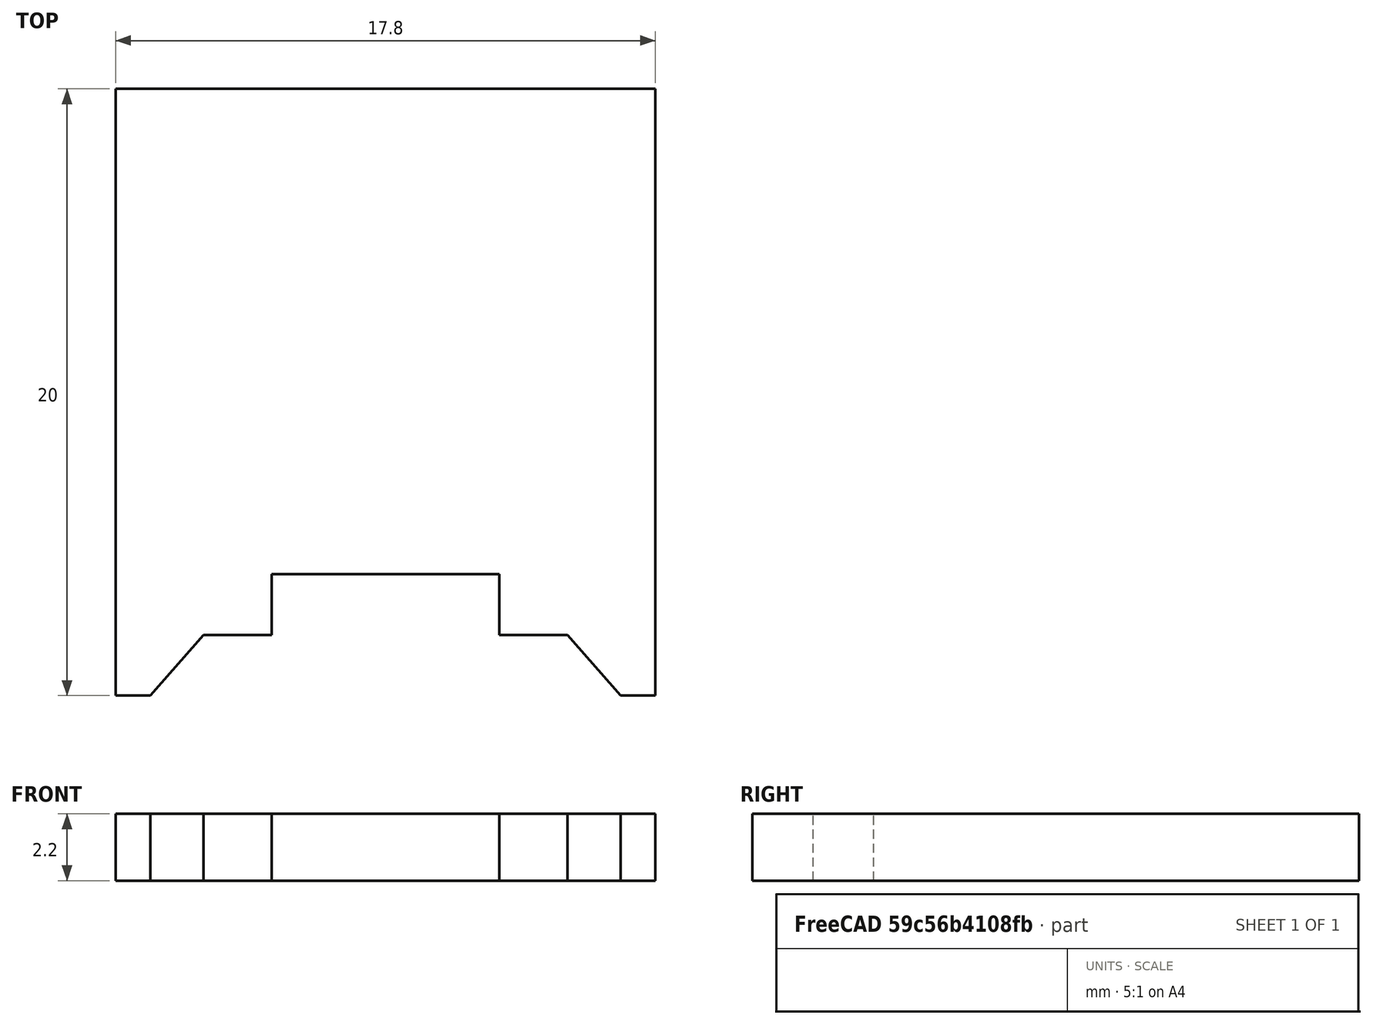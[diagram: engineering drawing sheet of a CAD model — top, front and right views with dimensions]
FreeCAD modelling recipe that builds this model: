
FCSTD DOCUMENT  (FreeCAD 0.19R)
Label: rs41 upper mark 3
License: All rights reserved
LicenseURL: http://en.wikipedia.org/wiki/All_rights_reserved
objects: Sketcher::SketchObject×1, PartDesign::Pad×1, PartDesign::Body×1
note: 4 computed .brp shape members not serialized (recipe doc carries the construction recipe); baked Part::Feature solids carry a one-line shape summary decoded from their .brp

FEATURE [Sketcher::SketchObject] Sketch
  FullyConstrained = true
  MapMode = 5
  Support = -> [XY_Plane]
  sketch-geometry (12):
    g0: LineSegment StartX=-3.75 StartY=-16 StartZ=0 EndX=3.75 EndY=-16 EndZ=0
    g1: LineSegment StartX=3.75 StartY=-16 StartZ=0 EndX=3.75 EndY=-18 EndZ=0
    g2: LineSegment StartX=3.75 StartY=-18 StartZ=0 EndX=6 EndY=-18 EndZ=0
    g3: LineSegment StartX=7.75 StartY=-20 StartZ=0 EndX=8.9 EndY=-20 EndZ=0
    g4: LineSegment StartX=-8.9 StartY=0 StartZ=0 EndX=-8.9 EndY=-20 EndZ=0
    g5: LineSegment StartX=-8.9 StartY=-20 StartZ=0 EndX=-7.75 EndY=-20 EndZ=0
    g6: LineSegment StartX=-7.75 StartY=-20 StartZ=0 EndX=-6 EndY=-18 EndZ=0
    g7: LineSegment StartX=-6 StartY=-18 StartZ=0 EndX=-3.75 EndY=-18 EndZ=0
    g8: LineSegment StartX=-3.75 StartY=-18 StartZ=0 EndX=-3.75 EndY=-16 EndZ=0
    g9: LineSegment StartX=6 StartY=-18 StartZ=0 EndX=7.75 EndY=-20 EndZ=0
    g10: LineSegment StartX=8.9 StartY=-20 StartZ=0 EndX=8.9 EndY=0 EndZ=0
    g11: LineSegment StartX=8.9 StartY=0 StartZ=0 EndX=-8.9 EndY=0 EndZ=0
  constraints (30):
    c: Coincident(g1,g0)
    c: Vertical(g1)
    c: Horizontal(g2)
    c: Horizontal(g3)
    c: Vertical(g4)
    c: Coincident(g5,g4)
    c: Coincident(g6,g5)
    c: Coincident(g7,g6)
    c: Coincident(g8,g7)
    c: Coincident(g8,g0)
    c: Coincident(g2,g1)
    c: Coincident(g9,g2)
    c: Coincident(g9,g3)
    c: Coincident(g10,g3)
    c: Coincident(g11,g10)
    c: Symmetric(g4,g10,g-2)
    c: Symmetric(g4,g3,g-2)
    c: Symmetric(g5,g3,g-2)
    c: Symmetric(g6,g2,g-2)
    c: Symmetric(g7,g1,g-2)
    c: Distance(g0) = 7.5
    c: DistanceX(g4,g10) = 17.8
    c: Distance(g8) = 2
    c: DistanceX(g6,g2) = 12
    c: DistanceX(g5,g3) = 15.5
    c: Distance(g10) = 20
    c: Symmetric(g0,g0,g-2)
    c: DistanceY(g3,g2) = 2
    c: Coincident(g4,g11)
    c: PointOnObject(g-1,g11)
FEATURE [PartDesign::Pad] Pad
  Direction = (1,1,1)
  Length = 2.2
  Length2 = 100
  Profile = -> Sketch
  Type = 0
FEATURE [PartDesign::Body] Body
  Group = -> [Sketch,Pad]
  Origin = -> Origin
  Tip = -> Pad
